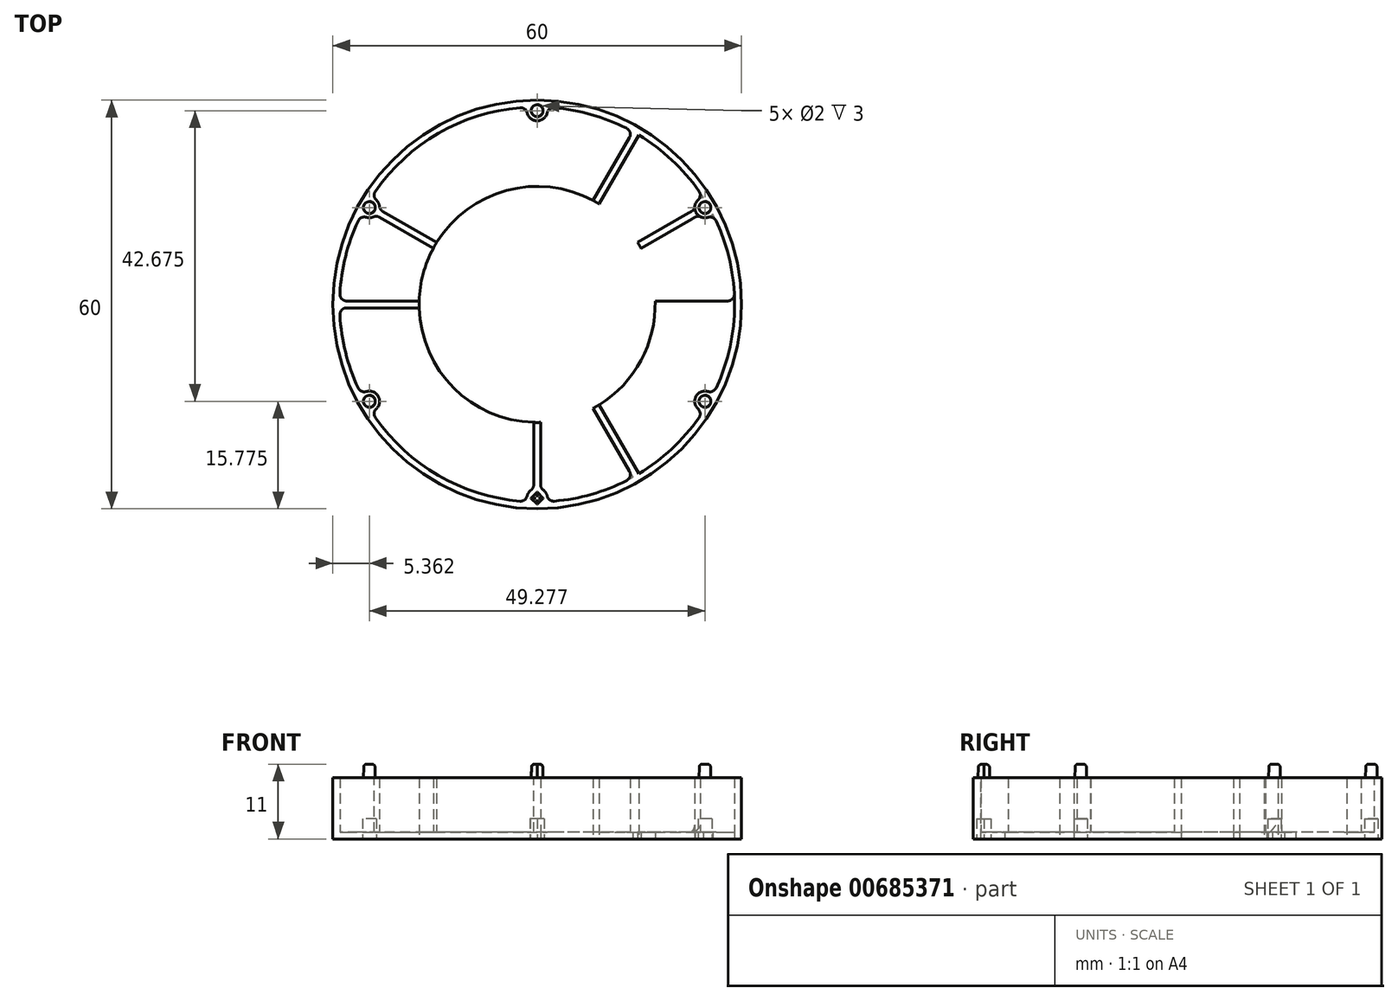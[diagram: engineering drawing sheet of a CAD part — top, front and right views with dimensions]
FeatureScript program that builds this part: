
annotation { "Feature Type Name" : "Feature", "Feature Type Description" : "" }
export const myFeature = defineFeature(function(context is Context, id is Id, definition is map)
    precondition{}
    {
        {
            var Q0;
            Q0=qCreatedBy(makeId("Top.planeOp"),FACE);
            var sketch = newSketch(context, id + "F0", { "sketchPlane" : qUnion([Q0])});
            skCircle(sketch, "E0", {"center": v(0, 0) * mm, "radius": 30 * mm});
            skCircle(sketch, "E1.0", {"center": v(0, 0) * mm, "radius": 29 * mm});
            skLineSegment(sketch, "E2.bottom", {"start": v(14.56, 26.23) * mm, "end": v(15.43, 25.73) * mm});
            skLineSegment(sketch, "E2.top", {"start": v(-15.43, -25.73) * mm, "end": v(-14.56, -26.23) * mm});
            skLineSegment(sketch, "E2.left", {"start": v(14.56, 26.23) * mm, "end": v(-15.43, -25.73) * mm});
            skLineSegment(sketch, "E2.right", {"start": v(15.43, 25.73) * mm, "end": v(-14.56, -26.23) * mm});
            skLineSegment(sketch, "E3.bottom", {"start": v(25.73, 15.43) * mm, "end": v(26.23, 14.56) * mm});
            skLineSegment(sketch, "E3.top", {"start": v(-26.23, -14.56) * mm, "end": v(-25.73, -15.43) * mm});
            skLineSegment(sketch, "E3.left", {"start": v(25.73, 15.43) * mm, "end": v(-26.23, -14.56) * mm});
            skLineSegment(sketch, "E3.right", {"start": v(26.23, 14.56) * mm, "end": v(-25.73, -15.43) * mm});
            skLineSegment(sketch, "E4", {"start": v(-38.35, 0) * mm, "end": v(39.17, 0) * mm, "construction": true});
            skLineSegment(sketch, "E5", {"start": v(0, 42.5) * mm, "end": v(0, -42.47) * mm, "construction": true});
            skLineSegment(sketch, "E6.bottom", {"start": v(-30, 0.5) * mm, "end": v(30, 0.5) * mm});
            skLineSegment(sketch, "E6.top", {"start": v(-30, -0.5) * mm, "end": v(30, -0.5) * mm});
            skLineSegment(sketch, "E6.left", {"start": v(-30, 0.5) * mm, "end": v(-30, -0.5) * mm});
            skLineSegment(sketch, "E6.right", {"start": v(30, 0.5) * mm, "end": v(30, -0.5) * mm});
            skLineSegment(sketch, "E7.bottom", {"start": v(-25.73, 15.43) * mm, "end": v(26.23, -14.56) * mm});
            skLineSegment(sketch, "E7.top", {"start": v(-26.23, 14.56) * mm, "end": v(25.73, -15.43) * mm});
            skLineSegment(sketch, "E7.left", {"start": v(-25.73, 15.43) * mm, "end": v(-26.23, 14.56) * mm});
            skLineSegment(sketch, "E7.right", {"start": v(26.23, -14.56) * mm, "end": v(25.73, -15.43) * mm});
            skLineSegment(sketch, "E8.bottom", {"start": v(-0.5, 30) * mm, "end": v(0.5, 30) * mm});
            skLineSegment(sketch, "E8.top", {"start": v(-0.5, -30) * mm, "end": v(0.5, -30) * mm});
            skLineSegment(sketch, "E8.left", {"start": v(-0.5, 30) * mm, "end": v(-0.5, -30) * mm});
            skLineSegment(sketch, "E8.right", {"start": v(0.5, 30) * mm, "end": v(0.5, -30) * mm});
            skLineSegment(sketch, "E9.bottom", {"start": v(-15.43, 25.73) * mm, "end": v(-14.56, 26.23) * mm});
            skLineSegment(sketch, "E9.top", {"start": v(14.56, -26.23) * mm, "end": v(15.43, -25.73) * mm});
            skLineSegment(sketch, "E9.left", {"start": v(-15.43, 25.73) * mm, "end": v(14.56, -26.23) * mm});
            skLineSegment(sketch, "E9.right", {"start": v(-14.56, 26.23) * mm, "end": v(15.43, -25.73) * mm});
            skCircle(sketch, "E10", {"center": v(0, 0) * mm, "radius": 17.33 * mm});
            skSolve(sketch);
        }
        {
            var Q0;
            Q0=qCreatedBy(makeId("Top.planeOp"),FACE);
            var sketch = newSketch(context, id + "F1", { "sketchPlane" : qUnion([Q0])});
            skCircle(sketch, "E11", {"center": v(0, 0) * mm, "radius": 30 * mm});
            skCircle(sketch, "E12", {"center": v(0, 0) * mm, "radius": 29 * mm});
            skSolve(sketch);
        }
        {
            var Q0;
            Q0=makeQuery(id+"F1.imprint","IMPRINT",FACE,{"disambiguationData":[TD([[makeQuery(id+"F1.imprint","IMPRINT",EDGE,{"derivedFrom":sQuery(id+"F1.wireOp",EDGE,"E11")}),1.0]])]});
            extrude(context, id + "F2", {"entities" : qUnion([Q0]), "depth" : 9 * mm, "offsetDistance" : 25 * mm});
        }
        {
            var Q0;
            {var subQ0=sQuery(id+"F0.wireOp",EDGE,"E7.bottom");var subQ1=sQuery(id+"F0.wireOp",EDGE,"E1.0");var subQ2=makeQuery(id+"F0.imprint","INTERSECT",VERTEX,{"disambiguationData":[OD(0.0)],"derivedFrom":[subQ1,subQ0]});Q0=makeQuery(id+"F0.imprint","IMPRINT",FACE,{"disambiguationData":[TD([[makeQuery(id+"F0.imprint","IMPRINT",EDGE,{"disambiguationData":[TD([[subQ2,-1.0]])],"derivedFrom":subQ1}),1.0]])]});}
            var Q1;
            {var subQ0=sQuery(id+"F0.wireOp",EDGE,"E2.right");var subQ1=sQuery(id+"F0.wireOp",EDGE,"E1.0");var subQ2=makeQuery(id+"F0.imprint","INTERSECT",VERTEX,{"disambiguationData":[OD(0.0)],"derivedFrom":[subQ1,subQ0]});Q1=makeQuery(id+"F0.imprint","IMPRINT",FACE,{"disambiguationData":[TD([[makeQuery(id+"F0.imprint","IMPRINT",EDGE,{"disambiguationData":[TD([[subQ2,-1.0]])],"derivedFrom":subQ1}),1.0]])]});}
            var Q2;
            {var subQ0=sQuery(id+"F0.wireOp",EDGE,"E8.left");var subQ1=sQuery(id+"F0.wireOp",EDGE,"E1.0");var subQ2=makeQuery(id+"F0.imprint","INTERSECT",VERTEX,{"disambiguationData":[OD(1.0)],"derivedFrom":[subQ1,subQ0]});Q2=makeQuery(id+"F0.imprint","IMPRINT",FACE,{"disambiguationData":[TD([[makeQuery(id+"F0.imprint","IMPRINT",EDGE,{"disambiguationData":[TD([[subQ2,-1.0]])],"derivedFrom":subQ1}),1.0]])]});}
            var Q3;
            {var subQ0=sQuery(id+"F0.wireOp",EDGE,"E9.left");var subQ1=sQuery(id+"F0.wireOp",EDGE,"E1.0");var subQ2=makeQuery(id+"F0.imprint","INTERSECT",VERTEX,{"disambiguationData":[OD(1.0)],"derivedFrom":[subQ1,subQ0]});Q3=makeQuery(id+"F0.imprint","IMPRINT",FACE,{"disambiguationData":[TD([[makeQuery(id+"F0.imprint","IMPRINT",EDGE,{"disambiguationData":[TD([[subQ2,-1.0]])],"derivedFrom":subQ1}),1.0]])]});}
            var Q4;
            {var subQ0=sQuery(id+"F0.wireOp",EDGE,"E6.bottom");var subQ1=sQuery(id+"F0.wireOp",EDGE,"E1.0");var subQ2=makeQuery(id+"F0.imprint","INTERSECT",VERTEX,{"disambiguationData":[OD(1.0)],"derivedFrom":[subQ1,subQ0]});Q4=makeQuery(id+"F0.imprint","IMPRINT",FACE,{"disambiguationData":[TD([[makeQuery(id+"F0.imprint","IMPRINT",EDGE,{"disambiguationData":[TD([[subQ2,-1.0]])],"derivedFrom":subQ1}),1.0]])]});}
            extrude(context, id + "F3", {"entities" : qUnion([Q0, Q1, Q2, Q3, Q4]), "operationType" : NewBodyOperationType.ADD, "depth" : 9 * mm, "offsetDistance" : 25 * mm});
        }
        {
            var Q0;
            Q0=makeQuery(id+"F1.imprint","IMPRINT",FACE,{"disambiguationData":[TD([[makeQuery(id+"F1.imprint","IMPRINT",EDGE,{"derivedFrom":sQuery(id+"F1.wireOp",EDGE,"E11")}),1.0]])]});
            var Q1;
            Q1=makeQuery(id+"F1.imprint","IMPRINT",FACE,{"disambiguationData":[TD([[makeQuery(id+"F1.imprint","IMPRINT",EDGE,{"derivedFrom":sQuery(id+"F1.wireOp",EDGE,"E12")}),1.0]])]});
            extrude(context, id + "F4", {"entities" : qUnion([Q0, Q1]), "operationType" : NewBodyOperationType.ADD, "depth" : 1 * mm, "offsetDistance" : 25 * mm});
        }
        {
            var Q0;
            {var subQ0=sQuery(id+"F0.wireOp",EDGE,"E8.right");var subQ1=sQuery(id+"F0.wireOp",EDGE,"E1.0");var subQ2=makeQuery(id+"F0.imprint","INTERSECT",VERTEX,{"disambiguationData":[OD(1.0)],"derivedFrom":[subQ1,subQ0]});Q0=makeQuery(id+"F0.imprint","IMPRINT",FACE,{"disambiguationData":[TD([[makeQuery(id+"F0.imprint","IMPRINT",EDGE,{"disambiguationData":[TD([[subQ2,-1.0]])],"derivedFrom":subQ1}),1.0]])]});}
            var Q1;
            {var subQ0=sQuery(id+"F0.wireOp",EDGE,"E3.right");var subQ1=sQuery(id+"F0.wireOp",EDGE,"E1.0");var subQ2=makeQuery(id+"F0.imprint","INTERSECT",VERTEX,{"disambiguationData":[OD(0.0)],"derivedFrom":[subQ1,subQ0]});Q1=makeQuery(id+"F0.imprint","IMPRINT",FACE,{"disambiguationData":[TD([[makeQuery(id+"F0.imprint","IMPRINT",EDGE,{"disambiguationData":[TD([[subQ2,1.0]])],"derivedFrom":subQ1}),1.0]])]});}
            var Q2;
            {var subQ0=sQuery(id+"F0.wireOp",EDGE,"E3.left");var subQ1=sQuery(id+"F0.wireOp",EDGE,"E1.0");var subQ2=makeQuery(id+"F0.imprint","INTERSECT",VERTEX,{"disambiguationData":[OD(0.0)],"derivedFrom":[subQ1,subQ0]});Q2=makeQuery(id+"F0.imprint","IMPRINT",FACE,{"disambiguationData":[TD([[makeQuery(id+"F0.imprint","IMPRINT",EDGE,{"disambiguationData":[TD([[subQ2,-1.0]])],"derivedFrom":subQ1}),1.0]])]});}
            extrude(context, id + "F5", {"entities" : qUnion([Q0, Q1, Q2]), "operationType" : NewBodyOperationType.REMOVE, "depth" : 1 * mm, "offsetDistance" : 25 * mm});
        }
        {
            var Q0;
            Q0=qCreatedBy(makeId("Top.planeOp"),FACE);
            var sketch = newSketch(context, id + "F6", { "sketchPlane" : qUnion([Q0])});
            skCircle(sketch, "E13", {"center": v(0, 0) * mm, "radius": 28.45 * mm});
            skLineSegment(sketch, "E14", {"start": v(0, 28.45) * mm, "end": v(0, -28.45) * mm, "construction": true});
            skLineSegment(sketch, "E15", {"start": v(24.64, 14.22) * mm, "end": v(0, 0) * mm, "construction": true});
            skLineSegment(sketch, "E16", {"start": v(14.23, 24.64) * mm, "end": v(0, 0) * mm, "construction": true});
            skLineSegment(sketch, "E17", {"start": v(0, 0) * mm, "end": v(28.45, 0) * mm, "construction": true});
            skLineSegment(sketch, "E18", {"start": v(0, 0) * mm, "end": v(24.64, -14.22) * mm, "construction": true});
            skLineSegment(sketch, "E19", {"start": v(0, 0) * mm, "end": v(14.23, -24.64) * mm, "construction": true});
            skLineSegment(sketch, "E20", {"start": v(0, 0) * mm, "end": v(-14.23, 24.64) * mm, "construction": true});
            skLineSegment(sketch, "E21", {"start": v(0, 0) * mm, "end": v(-24.64, 14.22) * mm, "construction": true});
            skLineSegment(sketch, "E22", {"start": v(0, 0) * mm, "end": v(-28.45, 0) * mm, "construction": true});
            skLineSegment(sketch, "E23", {"start": v(0, 0) * mm, "end": v(-24.64, -14.23) * mm, "construction": true});
            skLineSegment(sketch, "E24", {"start": v(0, 0) * mm, "end": v(-14.22, -24.64) * mm, "construction": true});
            skCircle(sketch, "E25", {"center": v(0, 28.45) * mm, "radius": 1.5 * mm});
            skCircle(sketch, "E26", {"center": v(24.64, 14.22) * mm, "radius": 1.5 * mm});
            skCircle(sketch, "E27", {"center": v(24.64, -14.22) * mm, "radius": 1.5 * mm});
            skCircle(sketch, "E28", {"center": v(0, -28.45) * mm, "radius": 1.5 * mm});
            skCircle(sketch, "E29", {"center": v(-24.64, -14.23) * mm, "radius": 1.5 * mm});
            skCircle(sketch, "E30", {"center": v(-24.64, 14.22) * mm, "radius": 1.5 * mm});
            skCircle(sketch, "E31", {"center": v(-24.64, 14.22) * mm, "radius": 1 * mm});
            skCircle(sketch, "E32", {"center": v(0, 28.45) * mm, "radius": 1 * mm});
            skCircle(sketch, "E33", {"center": v(24.64, 14.22) * mm, "radius": 1 * mm});
            skCircle(sketch, "E34", {"center": v(24.64, -14.22) * mm, "radius": 1 * mm});
            skCircle(sketch, "E35", {"center": v(-24.64, -14.23) * mm, "radius": 1 * mm});
            skLineSegment(sketch, "E36.bottom", {"start": v(1.06, -28.45) * mm, "end": v(0, -29.51) * mm});
            skLineSegment(sketch, "E36.top", {"start": v(0, -27.39) * mm, "end": v(-1.06, -28.45) * mm});
            skLineSegment(sketch, "E36.left", {"start": v(1.06, -28.45) * mm, "end": v(0, -27.39) * mm});
            skLineSegment(sketch, "E36.right", {"start": v(0, -29.51) * mm, "end": v(-1.06, -28.45) * mm});
            skSolve(sketch);
        }
        {
            var Q0;
            {var subQ0=sQuery(id+"F6.wireOp",EDGE,"E30");var subQ1=sQuery(id+"F6.wireOp",EDGE,"E13");var subQ2=makeQuery(id+"F6.imprint","INTERSECT",VERTEX,{"disambiguationData":[OD(0.0)],"derivedFrom":[subQ1,subQ0]});Q0=makeQuery(id+"F6.imprint","IMPRINT",FACE,{"disambiguationData":[TD([[makeQuery(id+"F6.imprint","IMPRINT",EDGE,{"disambiguationData":[TD([[subQ2,-1.0]])],"derivedFrom":subQ1}),1.0]])]});}
            var Q1;
            {var subQ0=sQuery(id+"F6.wireOp",EDGE,"E30");var subQ1=sQuery(id+"F6.wireOp",EDGE,"E13");var subQ2=makeQuery(id+"F6.imprint","INTERSECT",VERTEX,{"disambiguationData":[OD(0.0)],"derivedFrom":[subQ1,subQ0]});Q1=makeQuery(id+"F6.imprint","IMPRINT",FACE,{"disambiguationData":[TD([[makeQuery(id+"F6.imprint","IMPRINT",EDGE,{"disambiguationData":[TD([[subQ2,-1.0]])],"derivedFrom":subQ1}),-1.0]])]});}
            var Q2;
            {var subQ0=sQuery(id+"F6.wireOp",EDGE,"E25");var subQ1=sQuery(id+"F6.wireOp",EDGE,"E13");var subQ2=makeQuery(id+"F6.imprint","INTERSECT",VERTEX,{"disambiguationData":[OD(0.0)],"derivedFrom":[subQ1,subQ0]});Q2=makeQuery(id+"F6.imprint","IMPRINT",FACE,{"disambiguationData":[TD([[makeQuery(id+"F6.imprint","IMPRINT",EDGE,{"disambiguationData":[TD([[subQ2,-1.0]])],"derivedFrom":subQ1}),1.0]])]});}
            var Q3;
            {var subQ0=sQuery(id+"F6.wireOp",EDGE,"E25");var subQ1=sQuery(id+"F6.wireOp",EDGE,"E13");var subQ2=makeQuery(id+"F6.imprint","INTERSECT",VERTEX,{"disambiguationData":[OD(0.0)],"derivedFrom":[subQ1,subQ0]});Q3=makeQuery(id+"F6.imprint","IMPRINT",FACE,{"disambiguationData":[TD([[makeQuery(id+"F6.imprint","IMPRINT",EDGE,{"disambiguationData":[TD([[subQ2,-1.0]])],"derivedFrom":subQ1}),-1.0]])]});}
            var Q4;
            {var subQ0=sQuery(id+"F6.wireOp",EDGE,"E26");var subQ1=sQuery(id+"F6.wireOp",EDGE,"E13");var subQ2=makeQuery(id+"F6.imprint","INTERSECT",VERTEX,{"disambiguationData":[OD(0.0)],"derivedFrom":[subQ1,subQ0]});Q4=makeQuery(id+"F6.imprint","IMPRINT",FACE,{"disambiguationData":[TD([[makeQuery(id+"F6.imprint","IMPRINT",EDGE,{"disambiguationData":[TD([[subQ2,-1.0]])],"derivedFrom":subQ1}),-1.0]])]});}
            var Q5;
            {var subQ0=sQuery(id+"F6.wireOp",EDGE,"E26");var subQ1=sQuery(id+"F6.wireOp",EDGE,"E13");var subQ2=makeQuery(id+"F6.imprint","INTERSECT",VERTEX,{"disambiguationData":[OD(0.0)],"derivedFrom":[subQ1,subQ0]});Q5=makeQuery(id+"F6.imprint","IMPRINT",FACE,{"disambiguationData":[TD([[makeQuery(id+"F6.imprint","IMPRINT",EDGE,{"disambiguationData":[TD([[subQ2,-1.0]])],"derivedFrom":subQ1}),1.0]])]});}
            var Q6;
            {var subQ0=sQuery(id+"F6.wireOp",EDGE,"E29");var subQ1=sQuery(id+"F6.wireOp",EDGE,"E13");var subQ2=makeQuery(id+"F6.imprint","INTERSECT",VERTEX,{"disambiguationData":[OD(0.0)],"derivedFrom":[subQ1,subQ0]});Q6=makeQuery(id+"F6.imprint","IMPRINT",FACE,{"disambiguationData":[TD([[makeQuery(id+"F6.imprint","IMPRINT",EDGE,{"disambiguationData":[TD([[subQ2,-1.0]])],"derivedFrom":subQ1}),1.0]])]});}
            var Q7;
            {var subQ0=sQuery(id+"F6.wireOp",EDGE,"E29");var subQ1=sQuery(id+"F6.wireOp",EDGE,"E13");var subQ2=makeQuery(id+"F6.imprint","INTERSECT",VERTEX,{"disambiguationData":[OD(0.0)],"derivedFrom":[subQ1,subQ0]});Q7=makeQuery(id+"F6.imprint","IMPRINT",FACE,{"disambiguationData":[TD([[makeQuery(id+"F6.imprint","IMPRINT",EDGE,{"disambiguationData":[TD([[subQ2,-1.0]])],"derivedFrom":subQ1}),-1.0]])]});}
            var Q8;
            {var subQ3=sQuery(id+"F6.wireOp",EDGE,"E13");var subQ5=sQuery(id+"F6.wireOp",EDGE,"E28");var subQ6=makeQuery(id+"F6.imprint","INTERSECT",VERTEX,{"disambiguationData":[OD(0.0)],"derivedFrom":[subQ3,subQ5]});Q8=makeQuery(id+"F6.imprint","IMPRINT",FACE,{"disambiguationData":[TD([[makeQuery(id+"F6.imprint","IMPRINT",EDGE,{"disambiguationData":[TD([[subQ6,-1.0]])],"derivedFrom":subQ3}),1.0]])]});}
            var Q9;
            {var subQ6=sQuery(id+"F6.wireOp",EDGE,"E36.bottom");Q9=makeQuery(id+"F6.imprint","IMPRINT",FACE,{"disambiguationData":[TD([[makeQuery(id+"F6.imprint","IMPRINT",EDGE,{"derivedFrom":subQ6}),1.0]])]});}
            var Q10;
            {var subQ0=sQuery(id+"F6.wireOp",EDGE,"E27");var subQ1=sQuery(id+"F6.wireOp",EDGE,"E13");var subQ2=makeQuery(id+"F6.imprint","INTERSECT",VERTEX,{"disambiguationData":[OD(0.0)],"derivedFrom":[subQ1,subQ0]});Q10=makeQuery(id+"F6.imprint","IMPRINT",FACE,{"disambiguationData":[TD([[makeQuery(id+"F6.imprint","IMPRINT",EDGE,{"disambiguationData":[TD([[subQ2,-1.0]])],"derivedFrom":subQ1}),-1.0]])]});}
            var Q11;
            {var subQ0=sQuery(id+"F6.wireOp",EDGE,"E27");var subQ1=sQuery(id+"F6.wireOp",EDGE,"E13");var subQ2=makeQuery(id+"F6.imprint","INTERSECT",VERTEX,{"disambiguationData":[OD(0.0)],"derivedFrom":[subQ1,subQ0]});Q11=makeQuery(id+"F6.imprint","IMPRINT",FACE,{"disambiguationData":[TD([[makeQuery(id+"F6.imprint","IMPRINT",EDGE,{"disambiguationData":[TD([[subQ2,-1.0]])],"derivedFrom":subQ1}),1.0]])]});}
            var Q12;
            {var subQ0=sQuery(id+"F6.wireOp",EDGE,"E31");var subQ1=sQuery(id+"F6.wireOp",EDGE,"E13");var subQ2=makeQuery(id+"F6.imprint","INTERSECT",VERTEX,{"disambiguationData":[OD(0.0)],"derivedFrom":[subQ1,subQ0]});Q12=makeQuery(id+"F6.imprint","IMPRINT",FACE,{"disambiguationData":[TD([[makeQuery(id+"F6.imprint","IMPRINT",EDGE,{"disambiguationData":[TD([[subQ2,-1.0]])],"derivedFrom":subQ1}),1.0]])]});}
            var Q13;
            {var subQ0=sQuery(id+"F6.wireOp",EDGE,"E31");var subQ1=sQuery(id+"F6.wireOp",EDGE,"E13");var subQ2=makeQuery(id+"F6.imprint","INTERSECT",VERTEX,{"disambiguationData":[OD(0.0)],"derivedFrom":[subQ1,subQ0]});Q13=makeQuery(id+"F6.imprint","IMPRINT",FACE,{"disambiguationData":[TD([[makeQuery(id+"F6.imprint","IMPRINT",EDGE,{"disambiguationData":[TD([[subQ2,-1.0]])],"derivedFrom":subQ1}),-1.0]])]});}
            var Q14;
            {var subQ0=sQuery(id+"F6.wireOp",EDGE,"E32");var subQ1=sQuery(id+"F6.wireOp",EDGE,"E13");var subQ2=makeQuery(id+"F6.imprint","INTERSECT",VERTEX,{"disambiguationData":[OD(0.0)],"derivedFrom":[subQ1,subQ0]});Q14=makeQuery(id+"F6.imprint","IMPRINT",FACE,{"disambiguationData":[TD([[makeQuery(id+"F6.imprint","IMPRINT",EDGE,{"disambiguationData":[TD([[subQ2,-1.0]])],"derivedFrom":subQ1}),-1.0]])]});}
            var Q15;
            {var subQ0=sQuery(id+"F6.wireOp",EDGE,"E32");var subQ1=sQuery(id+"F6.wireOp",EDGE,"E13");var subQ2=makeQuery(id+"F6.imprint","INTERSECT",VERTEX,{"disambiguationData":[OD(0.0)],"derivedFrom":[subQ1,subQ0]});Q15=makeQuery(id+"F6.imprint","IMPRINT",FACE,{"disambiguationData":[TD([[makeQuery(id+"F6.imprint","IMPRINT",EDGE,{"disambiguationData":[TD([[subQ2,-1.0]])],"derivedFrom":subQ1}),1.0]])]});}
            var Q16;
            {var subQ0=sQuery(id+"F6.wireOp",EDGE,"E33");var subQ1=sQuery(id+"F6.wireOp",EDGE,"E13");var subQ2=makeQuery(id+"F6.imprint","INTERSECT",VERTEX,{"disambiguationData":[OD(0.0)],"derivedFrom":[subQ1,subQ0]});Q16=makeQuery(id+"F6.imprint","IMPRINT",FACE,{"disambiguationData":[TD([[makeQuery(id+"F6.imprint","IMPRINT",EDGE,{"disambiguationData":[TD([[subQ2,-1.0]])],"derivedFrom":subQ1}),-1.0]])]});}
            var Q17;
            {var subQ0=sQuery(id+"F6.wireOp",EDGE,"E33");var subQ1=sQuery(id+"F6.wireOp",EDGE,"E13");var subQ2=makeQuery(id+"F6.imprint","INTERSECT",VERTEX,{"disambiguationData":[OD(0.0)],"derivedFrom":[subQ1,subQ0]});Q17=makeQuery(id+"F6.imprint","IMPRINT",FACE,{"disambiguationData":[TD([[makeQuery(id+"F6.imprint","IMPRINT",EDGE,{"disambiguationData":[TD([[subQ2,-1.0]])],"derivedFrom":subQ1}),1.0]])]});}
            var Q18;
            {var subQ0=sQuery(id+"F6.wireOp",EDGE,"E34");var subQ1=sQuery(id+"F6.wireOp",EDGE,"E13");var subQ2=makeQuery(id+"F6.imprint","INTERSECT",VERTEX,{"disambiguationData":[OD(0.0)],"derivedFrom":[subQ1,subQ0]});Q18=makeQuery(id+"F6.imprint","IMPRINT",FACE,{"disambiguationData":[TD([[makeQuery(id+"F6.imprint","IMPRINT",EDGE,{"disambiguationData":[TD([[subQ2,-1.0]])],"derivedFrom":subQ1}),-1.0]])]});}
            var Q19;
            {var subQ0=sQuery(id+"F6.wireOp",EDGE,"E34");var subQ1=sQuery(id+"F6.wireOp",EDGE,"E13");var subQ2=makeQuery(id+"F6.imprint","INTERSECT",VERTEX,{"disambiguationData":[OD(0.0)],"derivedFrom":[subQ1,subQ0]});Q19=makeQuery(id+"F6.imprint","IMPRINT",FACE,{"disambiguationData":[TD([[makeQuery(id+"F6.imprint","IMPRINT",EDGE,{"disambiguationData":[TD([[subQ2,-1.0]])],"derivedFrom":subQ1}),1.0]])]});}
            var Q20;
            {var subQ1=sQuery(id+"F6.wireOp",EDGE,"E36.bottom");Q20=makeQuery(id+"F6.imprint","IMPRINT",FACE,{"disambiguationData":[TD([[makeQuery(id+"F6.imprint","IMPRINT",EDGE,{"derivedFrom":subQ1}),-1.0]])]});}
            var Q21;
            {var subQ0=sQuery(id+"F6.wireOp",EDGE,"E35");var subQ1=sQuery(id+"F6.wireOp",EDGE,"E13");var subQ2=makeQuery(id+"F6.imprint","INTERSECT",VERTEX,{"disambiguationData":[OD(0.0)],"derivedFrom":[subQ1,subQ0]});Q21=makeQuery(id+"F6.imprint","IMPRINT",FACE,{"disambiguationData":[TD([[makeQuery(id+"F6.imprint","IMPRINT",EDGE,{"disambiguationData":[TD([[subQ2,-1.0]])],"derivedFrom":subQ1}),-1.0]])]});}
            var Q22;
            {var subQ0=sQuery(id+"F6.wireOp",EDGE,"E35");var subQ1=sQuery(id+"F6.wireOp",EDGE,"E13");var subQ2=makeQuery(id+"F6.imprint","INTERSECT",VERTEX,{"disambiguationData":[OD(0.0)],"derivedFrom":[subQ1,subQ0]});Q22=makeQuery(id+"F6.imprint","IMPRINT",FACE,{"disambiguationData":[TD([[makeQuery(id+"F6.imprint","IMPRINT",EDGE,{"disambiguationData":[TD([[subQ2,-1.0]])],"derivedFrom":subQ1}),1.0]])]});}
            var Q23;
            {var subQ0=sQuery(id+"F6.wireOp",EDGE,"E36.top");var subQ1=sQuery(id+"F6.wireOp",EDGE,"E13");var subQ2=makeQuery(id+"F6.imprint","INTERSECT",VERTEX,{"derivedFrom":[subQ1,subQ0]});Q23=makeQuery(id+"F6.imprint","IMPRINT",FACE,{"disambiguationData":[TD([[makeQuery(id+"F6.imprint","IMPRINT",EDGE,{"disambiguationData":[TD([[subQ2,-1.0]])],"derivedFrom":subQ1}),1.0]])]});}
            extrude(context, id + "F7", {"entities" : qUnion([Q0, Q1, Q2, Q3, Q4, Q5, Q6, Q7, Q8, Q9, Q10, Q11, Q12, Q13, Q14, Q15, Q16, Q17, Q18, Q19, Q20, Q21, Q22, Q23]), "operationType" : NewBodyOperationType.ADD, "depth" : 9 * mm, "offsetDistance" : 25 * mm});
        }
        {
            var Q0;
            {var subQ0=sQuery(id+"F0.wireOp",EDGE,"E8.right");var subQ1=sQuery(id+"F0.wireOp",EDGE,"E1.0");Q0=makeQuery(id+"F3.opExtrude","SWEPT_EDGE",EDGE,{"disambiguationData":[OSD([subQ1,subQ0]),TDD([makeQuery(id+"F0.imprint","INTERSECT",VERTEX,{"disambiguationData":[OD(1.0)],"derivedFrom":[subQ1,subQ0]})])]});}
            var Q1;
            {var subQ0=sQuery(id+"F0.wireOp",EDGE,"E2.left");var subQ1=sQuery(id+"F0.wireOp",EDGE,"E1.0");Q1=makeQuery(id+"F3.opExtrude","SWEPT_EDGE",EDGE,{"disambiguationData":[OSD([subQ1,subQ0]),TDD([makeQuery(id+"F0.imprint","INTERSECT",VERTEX,{"disambiguationData":[OD(1.0)],"derivedFrom":[subQ1,subQ0]})])]});}
            var Q2;
            {var subQ0=sQuery(id+"F0.wireOp",EDGE,"E3.left");var subQ1=sQuery(id+"F0.wireOp",EDGE,"E1.0");Q2=makeQuery(id+"F3.opExtrude","SWEPT_EDGE",EDGE,{"disambiguationData":[OSD([subQ1,subQ0]),TDD([makeQuery(id+"F0.imprint","INTERSECT",VERTEX,{"disambiguationData":[OD(1.0)],"derivedFrom":[subQ1,subQ0]})])]});}
            var Q3;
            {var subQ0=sQuery(id+"F0.wireOp",EDGE,"E6.bottom");var subQ1=sQuery(id+"F0.wireOp",EDGE,"E1.0");Q3=makeQuery(id+"F3.opExtrude","SWEPT_EDGE",EDGE,{"disambiguationData":[OSD([subQ1,subQ0]),TDD([makeQuery(id+"F0.imprint","INTERSECT",VERTEX,{"disambiguationData":[OD(1.0)],"derivedFrom":[subQ1,subQ0]})])]});}
            var Q4;
            {var subQ0=sQuery(id+"F0.wireOp",EDGE,"E9.right");var subQ1=sQuery(id+"F0.wireOp",EDGE,"E1.0");Q4=makeQuery(id+"F3.opExtrude","SWEPT_EDGE",EDGE,{"disambiguationData":[OSD([subQ1,subQ0]),TDD([makeQuery(id+"F0.imprint","INTERSECT",VERTEX,{"disambiguationData":[OD(1.0)],"derivedFrom":[subQ1,subQ0]})])]});}
            var Q5;
            {var subQ0=sQuery(id+"F0.wireOp",EDGE,"E7.bottom");var subQ1=sQuery(id+"F0.wireOp",EDGE,"E1.0");Q5=makeQuery(id+"F3.opExtrude","SWEPT_EDGE",EDGE,{"disambiguationData":[OSD([subQ1,subQ0]),TDD([makeQuery(id+"F0.imprint","INTERSECT",VERTEX,{"disambiguationData":[OD(1.0)],"derivedFrom":[subQ1,subQ0]})])]});}
            var Q6;
            {var subQ0=sQuery(id+"F0.wireOp",EDGE,"E8.left");var subQ1=sQuery(id+"F0.wireOp",EDGE,"E1.0");Q6=makeQuery(id+"F3.opExtrude","SWEPT_EDGE",EDGE,{"disambiguationData":[OSD([subQ1,subQ0]),TDD([makeQuery(id+"F0.imprint","INTERSECT",VERTEX,{"disambiguationData":[OD(0.0)],"derivedFrom":[subQ1,subQ0]})])]});}
            var Q7;
            {var subQ0=sQuery(id+"F0.wireOp",EDGE,"E2.left");var subQ1=sQuery(id+"F0.wireOp",EDGE,"E1.0");Q7=makeQuery(id+"F3.opExtrude","SWEPT_EDGE",EDGE,{"disambiguationData":[OSD([subQ1,subQ0]),TDD([makeQuery(id+"F0.imprint","INTERSECT",VERTEX,{"disambiguationData":[OD(0.0)],"derivedFrom":[subQ1,subQ0]})])]});}
            var Q8;
            {var subQ0=sQuery(id+"F0.wireOp",EDGE,"E3.left");var subQ1=sQuery(id+"F0.wireOp",EDGE,"E1.0");Q8=makeQuery(id+"F3.opExtrude","SWEPT_EDGE",EDGE,{"disambiguationData":[OSD([subQ1,subQ0]),TDD([makeQuery(id+"F0.imprint","INTERSECT",VERTEX,{"disambiguationData":[OD(0.0)],"derivedFrom":[subQ1,subQ0]})])]});}
            var Q9;
            {var subQ0=sQuery(id+"F0.wireOp",EDGE,"E6.top");var subQ1=sQuery(id+"F0.wireOp",EDGE,"E1.0");Q9=makeQuery(id+"F3.opExtrude","SWEPT_EDGE",EDGE,{"disambiguationData":[OSD([subQ1,subQ0]),TDD([makeQuery(id+"F0.imprint","INTERSECT",VERTEX,{"disambiguationData":[OD(1.0)],"derivedFrom":[subQ1,subQ0]})])]});}
            var Q10;
            {var subQ0=sQuery(id+"F0.wireOp",EDGE,"E7.top");var subQ1=sQuery(id+"F0.wireOp",EDGE,"E1.0");Q10=makeQuery(id+"F3.opExtrude","SWEPT_EDGE",EDGE,{"disambiguationData":[OSD([subQ1,subQ0]),TDD([makeQuery(id+"F0.imprint","INTERSECT",VERTEX,{"disambiguationData":[OD(0.0)],"derivedFrom":[subQ1,subQ0]})])]});}
            var Q11;
            {var subQ0=sQuery(id+"F0.wireOp",EDGE,"E6.top");var subQ1=sQuery(id+"F0.wireOp",EDGE,"E1.0");Q11=makeQuery(id+"F3.opExtrude","SWEPT_EDGE",EDGE,{"disambiguationData":[OSD([subQ1,subQ0]),TDD([makeQuery(id+"F0.imprint","INTERSECT",VERTEX,{"disambiguationData":[OD(0.0)],"derivedFrom":[subQ1,subQ0]})])]});}
            var Q12;
            {var subQ0=sQuery(id+"F0.wireOp",EDGE,"E9.left");var subQ1=sQuery(id+"F0.wireOp",EDGE,"E1.0");Q12=makeQuery(id+"F3.opExtrude","SWEPT_EDGE",EDGE,{"disambiguationData":[OSD([subQ1,subQ0]),TDD([makeQuery(id+"F0.imprint","INTERSECT",VERTEX,{"disambiguationData":[OD(0.0)],"derivedFrom":[subQ1,subQ0]})])]});}
            var Q13;
            {var subQ0=sQuery(id+"F0.wireOp",EDGE,"E8.right");var subQ1=sQuery(id+"F0.wireOp",EDGE,"E1.0");Q13=makeQuery(id+"F3.opExtrude","SWEPT_EDGE",EDGE,{"disambiguationData":[OSD([subQ1,subQ0]),TDD([makeQuery(id+"F0.imprint","INTERSECT",VERTEX,{"disambiguationData":[OD(0.0)],"derivedFrom":[subQ1,subQ0]})])]});}
            var Q14;
            {var subQ0=sQuery(id+"F0.wireOp",EDGE,"E7.bottom");var subQ1=sQuery(id+"F0.wireOp",EDGE,"E1.0");Q14=makeQuery(id+"F3.opExtrude","SWEPT_EDGE",EDGE,{"disambiguationData":[OSD([subQ1,subQ0]),TDD([makeQuery(id+"F0.imprint","INTERSECT",VERTEX,{"disambiguationData":[OD(0.0)],"derivedFrom":[subQ1,subQ0]})])]});}
            var Q15;
            {var subQ0=sQuery(id+"F0.wireOp",EDGE,"E9.right");var subQ1=sQuery(id+"F0.wireOp",EDGE,"E1.0");Q15=makeQuery(id+"F3.opExtrude","SWEPT_EDGE",EDGE,{"disambiguationData":[OSD([subQ1,subQ0]),TDD([makeQuery(id+"F0.imprint","INTERSECT",VERTEX,{"disambiguationData":[OD(0.0)],"derivedFrom":[subQ1,subQ0]})])]});}
            var Q16;
            {var subQ0=sQuery(id+"F0.wireOp",EDGE,"E3.right");var subQ1=sQuery(id+"F0.wireOp",EDGE,"E1.0");Q16=makeQuery(id+"F3.opExtrude","SWEPT_EDGE",EDGE,{"disambiguationData":[OSD([subQ1,subQ0]),TDD([makeQuery(id+"F0.imprint","INTERSECT",VERTEX,{"disambiguationData":[OD(1.0)],"derivedFrom":[subQ1,subQ0]})])]});}
            var Q17;
            {var subQ0=sQuery(id+"F0.wireOp",EDGE,"E2.right");var subQ1=sQuery(id+"F0.wireOp",EDGE,"E1.0");Q17=makeQuery(id+"F3.opExtrude","SWEPT_EDGE",EDGE,{"disambiguationData":[OSD([subQ1,subQ0]),TDD([makeQuery(id+"F0.imprint","INTERSECT",VERTEX,{"disambiguationData":[OD(1.0)],"derivedFrom":[subQ1,subQ0]})])]});}
            var Q18;
            {var subQ0=sQuery(id+"F0.wireOp",EDGE,"E3.right");var subQ1=sQuery(id+"F0.wireOp",EDGE,"E1.0");Q18=makeQuery(id+"F3.opExtrude","SWEPT_EDGE",EDGE,{"disambiguationData":[OSD([subQ1,subQ0]),TDD([makeQuery(id+"F0.imprint","INTERSECT",VERTEX,{"disambiguationData":[OD(0.0)],"derivedFrom":[subQ1,subQ0]})])]});}
            var Q19;
            {var subQ0=sQuery(id+"F0.wireOp",EDGE,"E2.right");var subQ1=sQuery(id+"F0.wireOp",EDGE,"E1.0");Q19=makeQuery(id+"F3.opExtrude","SWEPT_EDGE",EDGE,{"disambiguationData":[OSD([subQ1,subQ0]),TDD([makeQuery(id+"F0.imprint","INTERSECT",VERTEX,{"disambiguationData":[OD(0.0)],"derivedFrom":[subQ1,subQ0]})])]});}
            var Q20;
            {var subQ0=sQuery(id+"F0.wireOp",EDGE,"E8.left");var subQ1=sQuery(id+"F0.wireOp",EDGE,"E1.0");Q20=makeQuery(id+"F3.opExtrude","SWEPT_EDGE",EDGE,{"disambiguationData":[OSD([subQ1,subQ0]),TDD([makeQuery(id+"F0.imprint","INTERSECT",VERTEX,{"disambiguationData":[OD(1.0)],"derivedFrom":[subQ1,subQ0]})])]});}
            var Q21;
            {var subQ0=sQuery(id+"F0.wireOp",EDGE,"E9.left");var subQ1=sQuery(id+"F0.wireOp",EDGE,"E1.0");Q21=makeQuery(id+"F3.opExtrude","SWEPT_EDGE",EDGE,{"disambiguationData":[OSD([subQ1,subQ0]),TDD([makeQuery(id+"F0.imprint","INTERSECT",VERTEX,{"disambiguationData":[OD(1.0)],"derivedFrom":[subQ1,subQ0]})])]});}
            var Q22;
            {var subQ0=sQuery(id+"F0.wireOp",EDGE,"E7.top");var subQ1=sQuery(id+"F0.wireOp",EDGE,"E1.0");Q22=makeQuery(id+"F3.opExtrude","SWEPT_EDGE",EDGE,{"disambiguationData":[OSD([subQ1,subQ0]),TDD([makeQuery(id+"F0.imprint","INTERSECT",VERTEX,{"disambiguationData":[OD(1.0)],"derivedFrom":[subQ1,subQ0]})])]});}
            var Q23;
            {var subQ0=sQuery(id+"F0.wireOp",EDGE,"E6.bottom");var subQ1=sQuery(id+"F0.wireOp",EDGE,"E1.0");Q23=makeQuery(id+"F3.opExtrude","SWEPT_EDGE",EDGE,{"disambiguationData":[OSD([subQ1,subQ0]),TDD([makeQuery(id+"F0.imprint","INTERSECT",VERTEX,{"disambiguationData":[OD(0.0)],"derivedFrom":[subQ1,subQ0]})])]});}
            var Q24;
            {var subQ5=sQuery(id+"F0.wireOp",EDGE,"E6.bottom");var subQ8=sQuery(id+"F1.wireOp",EDGE,"E12");Q24=makeQuery(id+"F7.boolean.opBoolean","INTERSECT",EDGE,{"derivedFrom":[makeQuery(id+"F3.boolean.opBoolean","SPLIT",FACE,{"disambiguationData":[TD([makeQuery(id+"F3.opExtrude","SWEPT_FACE",FACE,{"disambiguationData":[OSD([subQ5])]})])],"derivedFrom":makeQuery(id+"F2.opExtrude","SWEPT_FACE",FACE,{"disambiguationData":[OSD([subQ8])]})}),makeQuery(id+"F7.opExtrude","SWEPT_FACE",FACE,{"disambiguationData":[OSD([sQuery(id+"F6.wireOp",EDGE,"E30")])]})]});}
            var Q25;
            Q25=makeQuery(id+"F7.boolean.opBoolean","INTERSECT",EDGE,{"derivedFrom":[makeQuery(id+"F3.opExtrude","SWEPT_FACE",FACE,{"disambiguationData":[OSD([sQuery(id+"F0.wireOp",EDGE,"E7.top")])]}),makeQuery(id+"F7.opExtrude","SWEPT_FACE",FACE,{"disambiguationData":[OSD([sQuery(id+"F6.wireOp",EDGE,"E30")])]})]});
            var Q26;
            {var subQ0=sQuery(id+"F0.wireOp",EDGE,"E1.0");var subQ1=sQuery(id+"F0.wireOp",EDGE,"E2.right");var subQ9=sQuery(id+"F1.wireOp",EDGE,"E12");Q26=makeQuery(id+"F7.boolean.opBoolean","INTERSECT",EDGE,{"disambiguationData":[OD(0.0)],"derivedFrom":[makeQuery(id+"F5.boolean.opBoolean","MERGE",FACE,{"derivedFrom":[makeQuery(id+"F3.boolean.opBoolean","SPLIT",FACE,{"disambiguationData":[TD([makeQuery(id+"F3.opExtrude","SWEPT_FACE",FACE,{"disambiguationData":[OSD([subQ1])]})])],"derivedFrom":makeQuery(id+"F2.opExtrude","SWEPT_FACE",FACE,{"disambiguationData":[OSD([subQ9])]})}),makeQuery(id+"F5.opExtrude","SWEPT_FACE",FACE,{"disambiguationData":[OSD([subQ0]),TDD([makeQuery(id+"F0.imprint","IMPRINT",EDGE,{"disambiguationData":[TD([[makeQuery(id+"F0.imprint","INTERSECT",VERTEX,{"disambiguationData":[OD(0.0)],"derivedFrom":[subQ0,sQuery(id+"F0.wireOp",EDGE,"E3.right")]}),1.0]])],"derivedFrom":subQ0})])]}),makeQuery(id+"F5.opExtrude","SWEPT_FACE",FACE,{"disambiguationData":[OSD([subQ0]),TDD([makeQuery(id+"F0.imprint","IMPRINT",EDGE,{"disambiguationData":[TD([[makeQuery(id+"F0.imprint","INTERSECT",VERTEX,{"disambiguationData":[OD(0.0)],"derivedFrom":[subQ0,sQuery(id+"F0.wireOp",EDGE,"E3.left")]}),-1.0]])],"derivedFrom":subQ0})])]})]}),makeQuery(id+"F7.opExtrude","SWEPT_FACE",FACE,{"disambiguationData":[OSD([sQuery(id+"F6.wireOp",EDGE,"E26")])]})]});}
            var Q27;
            Q27=makeQuery(id+"F7.boolean.opBoolean","INTERSECT",EDGE,{"derivedFrom":[makeQuery(id+"F5.boolean.opBoolean","COPY",FACE,{"derivedFrom":makeQuery(id+"F5.opExtrude","SWEPT_FACE",FACE,{"disambiguationData":[OSD([sQuery(id+"F0.wireOp",EDGE,"E3.right")])]})}),makeQuery(id+"F7.opExtrude","SWEPT_FACE",FACE,{"disambiguationData":[OSD([sQuery(id+"F6.wireOp",EDGE,"E26")])]})]});
            var Q28;
            Q28=makeQuery(id+"F7.boolean.opBoolean","INTERSECT",EDGE,{"derivedFrom":[makeQuery(id+"F4.opExtrude","CAP_FACE",FACE,{"disambiguationData":[OSD([sQuery(id+"F1.wireOp",EDGE,"E11")])],"isStart":false}),makeQuery(id+"F7.opExtrude","SWEPT_FACE",FACE,{"disambiguationData":[OSD([sQuery(id+"F6.wireOp",EDGE,"E26")])]})]});
            var Q29;
            {var subQ8=sQuery(id+"F1.wireOp",EDGE,"E12");var subQ10=sQuery(id+"F0.wireOp",EDGE,"E2.left");Q29=makeQuery(id+"F7.boolean.opBoolean","INTERSECT",EDGE,{"disambiguationData":[OD(0.0)],"derivedFrom":[makeQuery(id+"F3.boolean.opBoolean","SPLIT",FACE,{"disambiguationData":[TD([makeQuery(id+"F3.opExtrude","SWEPT_FACE",FACE,{"disambiguationData":[OSD([subQ10])]})])],"derivedFrom":makeQuery(id+"F2.opExtrude","SWEPT_FACE",FACE,{"disambiguationData":[OSD([subQ8])]})}),makeQuery(id+"F7.opExtrude","SWEPT_FACE",FACE,{"disambiguationData":[OSD([sQuery(id+"F6.wireOp",EDGE,"E25")])]})]});}
            var Q30;
            {var subQ8=sQuery(id+"F1.wireOp",EDGE,"E12");var subQ10=sQuery(id+"F0.wireOp",EDGE,"E2.left");Q30=makeQuery(id+"F7.boolean.opBoolean","INTERSECT",EDGE,{"disambiguationData":[OD(1.0)],"derivedFrom":[makeQuery(id+"F3.boolean.opBoolean","SPLIT",FACE,{"disambiguationData":[TD([makeQuery(id+"F3.opExtrude","SWEPT_FACE",FACE,{"disambiguationData":[OSD([subQ10])]})])],"derivedFrom":makeQuery(id+"F2.opExtrude","SWEPT_FACE",FACE,{"disambiguationData":[OSD([subQ8])]})}),makeQuery(id+"F7.opExtrude","SWEPT_FACE",FACE,{"disambiguationData":[OSD([sQuery(id+"F6.wireOp",EDGE,"E25")])]})]});}
            var Q31;
            {var subQ0=sQuery(id+"F0.wireOp",EDGE,"E1.0");var subQ1=sQuery(id+"F0.wireOp",EDGE,"E2.right");var subQ9=sQuery(id+"F1.wireOp",EDGE,"E12");Q31=makeQuery(id+"F7.boolean.opBoolean","INTERSECT",EDGE,{"disambiguationData":[OD(1.0)],"derivedFrom":[makeQuery(id+"F5.boolean.opBoolean","MERGE",FACE,{"derivedFrom":[makeQuery(id+"F3.boolean.opBoolean","SPLIT",FACE,{"disambiguationData":[TD([makeQuery(id+"F3.opExtrude","SWEPT_FACE",FACE,{"disambiguationData":[OSD([subQ1])]})])],"derivedFrom":makeQuery(id+"F2.opExtrude","SWEPT_FACE",FACE,{"disambiguationData":[OSD([subQ9])]})}),makeQuery(id+"F5.opExtrude","SWEPT_FACE",FACE,{"disambiguationData":[OSD([subQ0]),TDD([makeQuery(id+"F0.imprint","IMPRINT",EDGE,{"disambiguationData":[TD([[makeQuery(id+"F0.imprint","INTERSECT",VERTEX,{"disambiguationData":[OD(0.0)],"derivedFrom":[subQ0,sQuery(id+"F0.wireOp",EDGE,"E3.right")]}),1.0]])],"derivedFrom":subQ0})])]}),makeQuery(id+"F5.opExtrude","SWEPT_FACE",FACE,{"disambiguationData":[OSD([subQ0]),TDD([makeQuery(id+"F0.imprint","IMPRINT",EDGE,{"disambiguationData":[TD([[makeQuery(id+"F0.imprint","INTERSECT",VERTEX,{"disambiguationData":[OD(0.0)],"derivedFrom":[subQ0,sQuery(id+"F0.wireOp",EDGE,"E3.left")]}),-1.0]])],"derivedFrom":subQ0})])]})]}),makeQuery(id+"F7.opExtrude","SWEPT_FACE",FACE,{"disambiguationData":[OSD([sQuery(id+"F6.wireOp",EDGE,"E26")])]})]});}
            var Q32;
            Q32=makeQuery(id+"F7.boolean.opBoolean","INTERSECT",EDGE,{"derivedFrom":[makeQuery(id+"F5.boolean.opBoolean","COPY",FACE,{"derivedFrom":makeQuery(id+"F5.opExtrude","SWEPT_FACE",FACE,{"disambiguationData":[OSD([sQuery(id+"F0.wireOp",EDGE,"E3.left")])]})}),makeQuery(id+"F7.opExtrude","SWEPT_FACE",FACE,{"disambiguationData":[OSD([sQuery(id+"F6.wireOp",EDGE,"E26")])]})]});
            var Q33;
            Q33=makeQuery(id+"F5.boolean.opBoolean","COPY",EDGE,{"derivedFrom":makeQuery(id+"F5.opExtrude","SWEPT_EDGE",EDGE,{"disambiguationData":[OSD([sQuery(id+"F0.wireOp",EDGE,"E1.0"),sQuery(id+"F0.wireOp",EDGE,"E6.bottom")])]})});
            var Q34;
            {var subQ0=sQuery(id+"F0.wireOp",EDGE,"E1.0");var subQ1=sQuery(id+"F0.wireOp",EDGE,"E2.right");var subQ9=sQuery(id+"F1.wireOp",EDGE,"E12");Q34=makeQuery(id+"F7.boolean.opBoolean","INTERSECT",EDGE,{"disambiguationData":[OD(1.0)],"derivedFrom":[makeQuery(id+"F5.boolean.opBoolean","MERGE",FACE,{"derivedFrom":[makeQuery(id+"F3.boolean.opBoolean","SPLIT",FACE,{"disambiguationData":[TD([makeQuery(id+"F3.opExtrude","SWEPT_FACE",FACE,{"disambiguationData":[OSD([subQ1])]})])],"derivedFrom":makeQuery(id+"F2.opExtrude","SWEPT_FACE",FACE,{"disambiguationData":[OSD([subQ9])]})}),makeQuery(id+"F5.opExtrude","SWEPT_FACE",FACE,{"disambiguationData":[OSD([subQ0]),TDD([makeQuery(id+"F0.imprint","IMPRINT",EDGE,{"disambiguationData":[TD([[makeQuery(id+"F0.imprint","INTERSECT",VERTEX,{"disambiguationData":[OD(0.0)],"derivedFrom":[subQ0,sQuery(id+"F0.wireOp",EDGE,"E3.right")]}),1.0]])],"derivedFrom":subQ0})])]}),makeQuery(id+"F5.opExtrude","SWEPT_FACE",FACE,{"disambiguationData":[OSD([subQ0]),TDD([makeQuery(id+"F0.imprint","IMPRINT",EDGE,{"disambiguationData":[TD([[makeQuery(id+"F0.imprint","INTERSECT",VERTEX,{"disambiguationData":[OD(0.0)],"derivedFrom":[subQ0,sQuery(id+"F0.wireOp",EDGE,"E3.left")]}),-1.0]])],"derivedFrom":subQ0})])]})]}),makeQuery(id+"F7.opExtrude","SWEPT_FACE",FACE,{"disambiguationData":[OSD([sQuery(id+"F6.wireOp",EDGE,"E27")])]})]});}
            var Q35;
            {var subQ0=sQuery(id+"F0.wireOp",EDGE,"E1.0");var subQ1=sQuery(id+"F0.wireOp",EDGE,"E2.right");var subQ9=sQuery(id+"F1.wireOp",EDGE,"E12");Q35=makeQuery(id+"F7.boolean.opBoolean","INTERSECT",EDGE,{"disambiguationData":[OD(0.0)],"derivedFrom":[makeQuery(id+"F5.boolean.opBoolean","MERGE",FACE,{"derivedFrom":[makeQuery(id+"F3.boolean.opBoolean","SPLIT",FACE,{"disambiguationData":[TD([makeQuery(id+"F3.opExtrude","SWEPT_FACE",FACE,{"disambiguationData":[OSD([subQ1])]})])],"derivedFrom":makeQuery(id+"F2.opExtrude","SWEPT_FACE",FACE,{"disambiguationData":[OSD([subQ9])]})}),makeQuery(id+"F5.opExtrude","SWEPT_FACE",FACE,{"disambiguationData":[OSD([subQ0]),TDD([makeQuery(id+"F0.imprint","IMPRINT",EDGE,{"disambiguationData":[TD([[makeQuery(id+"F0.imprint","INTERSECT",VERTEX,{"disambiguationData":[OD(0.0)],"derivedFrom":[subQ0,sQuery(id+"F0.wireOp",EDGE,"E3.right")]}),1.0]])],"derivedFrom":subQ0})])]}),makeQuery(id+"F5.opExtrude","SWEPT_FACE",FACE,{"disambiguationData":[OSD([subQ0]),TDD([makeQuery(id+"F0.imprint","IMPRINT",EDGE,{"disambiguationData":[TD([[makeQuery(id+"F0.imprint","INTERSECT",VERTEX,{"disambiguationData":[OD(0.0)],"derivedFrom":[subQ0,sQuery(id+"F0.wireOp",EDGE,"E3.left")]}),-1.0]])],"derivedFrom":subQ0})])]})]}),makeQuery(id+"F7.opExtrude","SWEPT_FACE",FACE,{"disambiguationData":[OSD([sQuery(id+"F6.wireOp",EDGE,"E27")])]})]});}
            var Q36;
            Q36=makeQuery(id+"F7.boolean.opBoolean","INTERSECT",EDGE,{"derivedFrom":[makeQuery(id+"F3.opExtrude","SWEPT_FACE",FACE,{"disambiguationData":[OSD([sQuery(id+"F0.wireOp",EDGE,"E7.bottom")])]}),makeQuery(id+"F7.opExtrude","SWEPT_FACE",FACE,{"disambiguationData":[OSD([sQuery(id+"F6.wireOp",EDGE,"E30")])]})]});
            var Q37;
            {var subQ8=sQuery(id+"F1.wireOp",EDGE,"E12");var subQ10=sQuery(id+"F0.wireOp",EDGE,"E2.left");Q37=makeQuery(id+"F7.boolean.opBoolean","INTERSECT",EDGE,{"derivedFrom":[makeQuery(id+"F3.boolean.opBoolean","SPLIT",FACE,{"disambiguationData":[TD([makeQuery(id+"F3.opExtrude","SWEPT_FACE",FACE,{"disambiguationData":[OSD([subQ10])]})])],"derivedFrom":makeQuery(id+"F2.opExtrude","SWEPT_FACE",FACE,{"disambiguationData":[OSD([subQ8])]})}),makeQuery(id+"F7.opExtrude","SWEPT_FACE",FACE,{"disambiguationData":[OSD([sQuery(id+"F6.wireOp",EDGE,"E30")])]})]});}
            var Q38;
            {var subQ4=sQuery(id+"F0.wireOp",EDGE,"E6.top");var subQ8=sQuery(id+"F1.wireOp",EDGE,"E12");Q38=makeQuery(id+"F7.boolean.opBoolean","INTERSECT",EDGE,{"disambiguationData":[OD(0.0)],"derivedFrom":[makeQuery(id+"F3.boolean.opBoolean","SPLIT",FACE,{"disambiguationData":[TD([makeQuery(id+"F3.opExtrude","SWEPT_FACE",FACE,{"disambiguationData":[OSD([subQ4])]})])],"derivedFrom":makeQuery(id+"F2.opExtrude","SWEPT_FACE",FACE,{"disambiguationData":[OSD([subQ8])]})}),makeQuery(id+"F7.opExtrude","SWEPT_FACE",FACE,{"disambiguationData":[OSD([sQuery(id+"F6.wireOp",EDGE,"E29")])]})]});}
            var Q39;
            {var subQ4=sQuery(id+"F0.wireOp",EDGE,"E6.top");var subQ8=sQuery(id+"F1.wireOp",EDGE,"E12");Q39=makeQuery(id+"F7.boolean.opBoolean","INTERSECT",EDGE,{"disambiguationData":[OD(1.0)],"derivedFrom":[makeQuery(id+"F3.boolean.opBoolean","SPLIT",FACE,{"disambiguationData":[TD([makeQuery(id+"F3.opExtrude","SWEPT_FACE",FACE,{"disambiguationData":[OSD([subQ4])]})])],"derivedFrom":makeQuery(id+"F2.opExtrude","SWEPT_FACE",FACE,{"disambiguationData":[OSD([subQ8])]})}),makeQuery(id+"F7.opExtrude","SWEPT_FACE",FACE,{"disambiguationData":[OSD([sQuery(id+"F6.wireOp",EDGE,"E29")])]})]});}
            var Q40;
            {var subQ0=sQuery(id+"F0.wireOp",EDGE,"E8.right");Q40=makeQuery(id+"F7.boolean.opBoolean","INTERSECT",EDGE,{"derivedFrom":[makeQuery(id+"F5.boolean.opBoolean","MERGE",FACE,{"derivedFrom":[makeQuery(id+"F3.opExtrude","SWEPT_FACE",FACE,{"disambiguationData":[OSD([subQ0])]}),makeQuery(id+"F5.opExtrude","SWEPT_FACE",FACE,{"disambiguationData":[OSD([subQ0])]})]}),makeQuery(id+"F7.opExtrude","SWEPT_FACE",FACE,{"disambiguationData":[OSD([sQuery(id+"F6.wireOp",EDGE,"E28")])]})]});}
            var Q41;
            {var subQ0=sQuery(id+"F0.wireOp",EDGE,"E8.right");var subQ1=sQuery(id+"F0.wireOp",EDGE,"E1.0");var subQ9=sQuery(id+"F1.wireOp",EDGE,"E12");Q41=makeQuery(id+"F7.boolean.opBoolean","INTERSECT",EDGE,{"derivedFrom":[makeQuery(id+"F5.boolean.opBoolean","MERGE",FACE,{"derivedFrom":[makeQuery(id+"F3.boolean.opBoolean","SPLIT",FACE,{"disambiguationData":[TD([makeQuery(id+"F3.opExtrude","SWEPT_FACE",FACE,{"disambiguationData":[OSD([subQ0])]})])],"derivedFrom":makeQuery(id+"F2.opExtrude","SWEPT_FACE",FACE,{"disambiguationData":[OSD([subQ9])]})}),makeQuery(id+"F5.opExtrude","SWEPT_FACE",FACE,{"disambiguationData":[OSD([subQ1]),TDD([makeQuery(id+"F0.imprint","IMPRINT",EDGE,{"disambiguationData":[TD([[makeQuery(id+"F0.imprint","INTERSECT",VERTEX,{"disambiguationData":[OD(1.0)],"derivedFrom":[subQ1,subQ0]}),-1.0]])],"derivedFrom":subQ1})])]})]}),makeQuery(id+"F7.opExtrude","SWEPT_FACE",FACE,{"disambiguationData":[OSD([sQuery(id+"F6.wireOp",EDGE,"E28")])]})]});}
            var Q42;
            {var subQ4=sQuery(id+"F0.wireOp",EDGE,"E6.top");var subQ8=sQuery(id+"F1.wireOp",EDGE,"E12");Q42=makeQuery(id+"F7.boolean.opBoolean","INTERSECT",EDGE,{"derivedFrom":[makeQuery(id+"F3.boolean.opBoolean","SPLIT",FACE,{"disambiguationData":[TD([makeQuery(id+"F3.opExtrude","SWEPT_FACE",FACE,{"disambiguationData":[OSD([subQ4])]})])],"derivedFrom":makeQuery(id+"F2.opExtrude","SWEPT_FACE",FACE,{"disambiguationData":[OSD([subQ8])]})}),makeQuery(id+"F7.opExtrude","SWEPT_FACE",FACE,{"disambiguationData":[OSD([sQuery(id+"F6.wireOp",EDGE,"E28")])]})]});}
            var Q43;
            Q43=makeQuery(id+"F7.boolean.opBoolean","INTERSECT",EDGE,{"derivedFrom":[makeQuery(id+"F3.opExtrude","SWEPT_FACE",FACE,{"disambiguationData":[OSD([sQuery(id+"F0.wireOp",EDGE,"E8.left")])]}),makeQuery(id+"F7.opExtrude","SWEPT_FACE",FACE,{"disambiguationData":[OSD([sQuery(id+"F6.wireOp",EDGE,"E28")])]})]});
            fillet(context, id + "F8", {"entities" : qUnion([Q0, Q1, Q2, Q3, Q4, Q5, Q6, Q7, Q8, Q9, Q10, Q11, Q12, Q13, Q14, Q15, Q16, Q17, Q18, Q19, Q20, Q21, Q22, Q23, Q24, Q25, Q26, Q27, Q28, Q29, Q30, Q31, Q32, Q33, Q34, Q35, Q36, Q37, Q38, Q39, Q40, Q41, Q42, Q43]), "radius" : 1 * mm, "tangentPropagation" : true, "allowEdgeOverflow" : false});
        }
        {
            var Q0;
            {var subQ0=sQuery(id+"F6.wireOp",EDGE,"E31");var subQ1=sQuery(id+"F6.wireOp",EDGE,"E13");var subQ2=makeQuery(id+"F6.imprint","INTERSECT",VERTEX,{"disambiguationData":[OD(0.0)],"derivedFrom":[subQ1,subQ0]});Q0=makeQuery(id+"F6.imprint","IMPRINT",FACE,{"disambiguationData":[TD([[makeQuery(id+"F6.imprint","IMPRINT",EDGE,{"disambiguationData":[TD([[subQ2,-1.0]])],"derivedFrom":subQ1}),-1.0]])]});}
            var Q1;
            {var subQ0=sQuery(id+"F6.wireOp",EDGE,"E31");var subQ1=sQuery(id+"F6.wireOp",EDGE,"E13");var subQ2=makeQuery(id+"F6.imprint","INTERSECT",VERTEX,{"disambiguationData":[OD(0.0)],"derivedFrom":[subQ1,subQ0]});Q1=makeQuery(id+"F6.imprint","IMPRINT",FACE,{"disambiguationData":[TD([[makeQuery(id+"F6.imprint","IMPRINT",EDGE,{"disambiguationData":[TD([[subQ2,-1.0]])],"derivedFrom":subQ1}),1.0]])]});}
            var Q2;
            {var subQ0=sQuery(id+"F6.wireOp",EDGE,"E32");var subQ1=sQuery(id+"F6.wireOp",EDGE,"E13");var subQ2=makeQuery(id+"F6.imprint","INTERSECT",VERTEX,{"disambiguationData":[OD(0.0)],"derivedFrom":[subQ1,subQ0]});Q2=makeQuery(id+"F6.imprint","IMPRINT",FACE,{"disambiguationData":[TD([[makeQuery(id+"F6.imprint","IMPRINT",EDGE,{"disambiguationData":[TD([[subQ2,-1.0]])],"derivedFrom":subQ1}),-1.0]])]});}
            var Q3;
            {var subQ0=sQuery(id+"F6.wireOp",EDGE,"E32");var subQ1=sQuery(id+"F6.wireOp",EDGE,"E13");var subQ2=makeQuery(id+"F6.imprint","INTERSECT",VERTEX,{"disambiguationData":[OD(0.0)],"derivedFrom":[subQ1,subQ0]});Q3=makeQuery(id+"F6.imprint","IMPRINT",FACE,{"disambiguationData":[TD([[makeQuery(id+"F6.imprint","IMPRINT",EDGE,{"disambiguationData":[TD([[subQ2,-1.0]])],"derivedFrom":subQ1}),1.0]])]});}
            var Q4;
            {var subQ0=sQuery(id+"F6.wireOp",EDGE,"E33");var subQ1=sQuery(id+"F6.wireOp",EDGE,"E13");var subQ2=makeQuery(id+"F6.imprint","INTERSECT",VERTEX,{"disambiguationData":[OD(0.0)],"derivedFrom":[subQ1,subQ0]});Q4=makeQuery(id+"F6.imprint","IMPRINT",FACE,{"disambiguationData":[TD([[makeQuery(id+"F6.imprint","IMPRINT",EDGE,{"disambiguationData":[TD([[subQ2,-1.0]])],"derivedFrom":subQ1}),1.0]])]});}
            var Q5;
            {var subQ0=sQuery(id+"F6.wireOp",EDGE,"E33");var subQ1=sQuery(id+"F6.wireOp",EDGE,"E13");var subQ2=makeQuery(id+"F6.imprint","INTERSECT",VERTEX,{"disambiguationData":[OD(0.0)],"derivedFrom":[subQ1,subQ0]});Q5=makeQuery(id+"F6.imprint","IMPRINT",FACE,{"disambiguationData":[TD([[makeQuery(id+"F6.imprint","IMPRINT",EDGE,{"disambiguationData":[TD([[subQ2,-1.0]])],"derivedFrom":subQ1}),-1.0]])]});}
            var Q6;
            {var subQ0=sQuery(id+"F6.wireOp",EDGE,"E34");var subQ1=sQuery(id+"F6.wireOp",EDGE,"E13");var subQ2=makeQuery(id+"F6.imprint","INTERSECT",VERTEX,{"disambiguationData":[OD(0.0)],"derivedFrom":[subQ1,subQ0]});Q6=makeQuery(id+"F6.imprint","IMPRINT",FACE,{"disambiguationData":[TD([[makeQuery(id+"F6.imprint","IMPRINT",EDGE,{"disambiguationData":[TD([[subQ2,-1.0]])],"derivedFrom":subQ1}),1.0]])]});}
            var Q7;
            {var subQ0=sQuery(id+"F6.wireOp",EDGE,"E34");var subQ1=sQuery(id+"F6.wireOp",EDGE,"E13");var subQ2=makeQuery(id+"F6.imprint","INTERSECT",VERTEX,{"disambiguationData":[OD(0.0)],"derivedFrom":[subQ1,subQ0]});Q7=makeQuery(id+"F6.imprint","IMPRINT",FACE,{"disambiguationData":[TD([[makeQuery(id+"F6.imprint","IMPRINT",EDGE,{"disambiguationData":[TD([[subQ2,-1.0]])],"derivedFrom":subQ1}),-1.0]])]});}
            var Q8;
            {var subQ1=sQuery(id+"F6.wireOp",EDGE,"E36.bottom");Q8=makeQuery(id+"F6.imprint","IMPRINT",FACE,{"disambiguationData":[TD([[makeQuery(id+"F6.imprint","IMPRINT",EDGE,{"derivedFrom":subQ1}),-1.0]])]});}
            var Q9;
            {var subQ0=sQuery(id+"F6.wireOp",EDGE,"E36.top");var subQ1=sQuery(id+"F6.wireOp",EDGE,"E13");var subQ2=makeQuery(id+"F6.imprint","INTERSECT",VERTEX,{"derivedFrom":[subQ1,subQ0]});Q9=makeQuery(id+"F6.imprint","IMPRINT",FACE,{"disambiguationData":[TD([[makeQuery(id+"F6.imprint","IMPRINT",EDGE,{"disambiguationData":[TD([[subQ2,-1.0]])],"derivedFrom":subQ1}),1.0]])]});}
            var Q10;
            {var subQ0=sQuery(id+"F6.wireOp",EDGE,"E35");var subQ1=sQuery(id+"F6.wireOp",EDGE,"E13");var subQ2=makeQuery(id+"F6.imprint","INTERSECT",VERTEX,{"disambiguationData":[OD(0.0)],"derivedFrom":[subQ1,subQ0]});Q10=makeQuery(id+"F6.imprint","IMPRINT",FACE,{"disambiguationData":[TD([[makeQuery(id+"F6.imprint","IMPRINT",EDGE,{"disambiguationData":[TD([[subQ2,-1.0]])],"derivedFrom":subQ1}),-1.0]])]});}
            var Q11;
            {var subQ0=sQuery(id+"F6.wireOp",EDGE,"E35");var subQ1=sQuery(id+"F6.wireOp",EDGE,"E13");var subQ2=makeQuery(id+"F6.imprint","INTERSECT",VERTEX,{"disambiguationData":[OD(0.0)],"derivedFrom":[subQ1,subQ0]});Q11=makeQuery(id+"F6.imprint","IMPRINT",FACE,{"disambiguationData":[TD([[makeQuery(id+"F6.imprint","IMPRINT",EDGE,{"disambiguationData":[TD([[subQ2,-1.0]])],"derivedFrom":subQ1}),1.0]])]});}
            extrude(context, id + "F9", {"entities" : qUnion([Q0, Q1, Q2, Q3, Q4, Q5, Q6, Q7, Q8, Q9, Q10, Q11]), "operationType" : NewBodyOperationType.ADD, "depth" : 11 * mm, "offsetDistance" : 25 * mm, "hasDraft" : true, "draftAngle" : .9 * degree, "draftPullDirection" : true});
        }
        {
            var Q0;
            {var subQ0=sQuery(id+"F6.wireOp",EDGE,"E35");var subQ1=sQuery(id+"F6.wireOp",EDGE,"E13");var subQ2=makeQuery(id+"F6.imprint","INTERSECT",VERTEX,{"disambiguationData":[OD(0.0)],"derivedFrom":[subQ1,subQ0]});Q0=makeQuery(id+"F6.imprint","IMPRINT",FACE,{"disambiguationData":[TD([[makeQuery(id+"F6.imprint","IMPRINT",EDGE,{"disambiguationData":[TD([[subQ2,-1.0]])],"derivedFrom":subQ1}),-1.0]])]});}
            var Q1;
            {var subQ0=sQuery(id+"F6.wireOp",EDGE,"E35");var subQ1=sQuery(id+"F6.wireOp",EDGE,"E13");var subQ2=makeQuery(id+"F6.imprint","INTERSECT",VERTEX,{"disambiguationData":[OD(0.0)],"derivedFrom":[subQ1,subQ0]});Q1=makeQuery(id+"F6.imprint","IMPRINT",FACE,{"disambiguationData":[TD([[makeQuery(id+"F6.imprint","IMPRINT",EDGE,{"disambiguationData":[TD([[subQ2,-1.0]])],"derivedFrom":subQ1}),1.0]])]});}
            var Q2;
            {var subQ1=sQuery(id+"F6.wireOp",EDGE,"E36.bottom");Q2=makeQuery(id+"F6.imprint","IMPRINT",FACE,{"disambiguationData":[TD([[makeQuery(id+"F6.imprint","IMPRINT",EDGE,{"derivedFrom":subQ1}),-1.0]])]});}
            var Q3;
            {var subQ0=sQuery(id+"F6.wireOp",EDGE,"E36.top");var subQ1=sQuery(id+"F6.wireOp",EDGE,"E13");var subQ2=makeQuery(id+"F6.imprint","INTERSECT",VERTEX,{"derivedFrom":[subQ1,subQ0]});Q3=makeQuery(id+"F6.imprint","IMPRINT",FACE,{"disambiguationData":[TD([[makeQuery(id+"F6.imprint","IMPRINT",EDGE,{"disambiguationData":[TD([[subQ2,-1.0]])],"derivedFrom":subQ1}),1.0]])]});}
            var Q4;
            {var subQ0=sQuery(id+"F6.wireOp",EDGE,"E34");var subQ1=sQuery(id+"F6.wireOp",EDGE,"E13");var subQ2=makeQuery(id+"F6.imprint","INTERSECT",VERTEX,{"disambiguationData":[OD(0.0)],"derivedFrom":[subQ1,subQ0]});Q4=makeQuery(id+"F6.imprint","IMPRINT",FACE,{"disambiguationData":[TD([[makeQuery(id+"F6.imprint","IMPRINT",EDGE,{"disambiguationData":[TD([[subQ2,-1.0]])],"derivedFrom":subQ1}),1.0]])]});}
            var Q5;
            {var subQ0=sQuery(id+"F6.wireOp",EDGE,"E34");var subQ1=sQuery(id+"F6.wireOp",EDGE,"E13");var subQ2=makeQuery(id+"F6.imprint","INTERSECT",VERTEX,{"disambiguationData":[OD(0.0)],"derivedFrom":[subQ1,subQ0]});Q5=makeQuery(id+"F6.imprint","IMPRINT",FACE,{"disambiguationData":[TD([[makeQuery(id+"F6.imprint","IMPRINT",EDGE,{"disambiguationData":[TD([[subQ2,-1.0]])],"derivedFrom":subQ1}),-1.0]])]});}
            var Q6;
            {var subQ0=sQuery(id+"F6.wireOp",EDGE,"E33");var subQ1=sQuery(id+"F6.wireOp",EDGE,"E13");var subQ2=makeQuery(id+"F6.imprint","INTERSECT",VERTEX,{"disambiguationData":[OD(0.0)],"derivedFrom":[subQ1,subQ0]});Q6=makeQuery(id+"F6.imprint","IMPRINT",FACE,{"disambiguationData":[TD([[makeQuery(id+"F6.imprint","IMPRINT",EDGE,{"disambiguationData":[TD([[subQ2,-1.0]])],"derivedFrom":subQ1}),1.0]])]});}
            var Q7;
            {var subQ0=sQuery(id+"F6.wireOp",EDGE,"E33");var subQ1=sQuery(id+"F6.wireOp",EDGE,"E13");var subQ2=makeQuery(id+"F6.imprint","INTERSECT",VERTEX,{"disambiguationData":[OD(0.0)],"derivedFrom":[subQ1,subQ0]});Q7=makeQuery(id+"F6.imprint","IMPRINT",FACE,{"disambiguationData":[TD([[makeQuery(id+"F6.imprint","IMPRINT",EDGE,{"disambiguationData":[TD([[subQ2,-1.0]])],"derivedFrom":subQ1}),-1.0]])]});}
            var Q8;
            {var subQ0=sQuery(id+"F6.wireOp",EDGE,"E32");var subQ1=sQuery(id+"F6.wireOp",EDGE,"E13");var subQ2=makeQuery(id+"F6.imprint","INTERSECT",VERTEX,{"disambiguationData":[OD(0.0)],"derivedFrom":[subQ1,subQ0]});Q8=makeQuery(id+"F6.imprint","IMPRINT",FACE,{"disambiguationData":[TD([[makeQuery(id+"F6.imprint","IMPRINT",EDGE,{"disambiguationData":[TD([[subQ2,-1.0]])],"derivedFrom":subQ1}),1.0]])]});}
            var Q9;
            {var subQ0=sQuery(id+"F6.wireOp",EDGE,"E32");var subQ1=sQuery(id+"F6.wireOp",EDGE,"E13");var subQ2=makeQuery(id+"F6.imprint","INTERSECT",VERTEX,{"disambiguationData":[OD(0.0)],"derivedFrom":[subQ1,subQ0]});Q9=makeQuery(id+"F6.imprint","IMPRINT",FACE,{"disambiguationData":[TD([[makeQuery(id+"F6.imprint","IMPRINT",EDGE,{"disambiguationData":[TD([[subQ2,-1.0]])],"derivedFrom":subQ1}),-1.0]])]});}
            var Q10;
            {var subQ0=sQuery(id+"F6.wireOp",EDGE,"E31");var subQ1=sQuery(id+"F6.wireOp",EDGE,"E13");var subQ2=makeQuery(id+"F6.imprint","INTERSECT",VERTEX,{"disambiguationData":[OD(0.0)],"derivedFrom":[subQ1,subQ0]});Q10=makeQuery(id+"F6.imprint","IMPRINT",FACE,{"disambiguationData":[TD([[makeQuery(id+"F6.imprint","IMPRINT",EDGE,{"disambiguationData":[TD([[subQ2,-1.0]])],"derivedFrom":subQ1}),-1.0]])]});}
            var Q11;
            {var subQ0=sQuery(id+"F6.wireOp",EDGE,"E31");var subQ1=sQuery(id+"F6.wireOp",EDGE,"E13");var subQ2=makeQuery(id+"F6.imprint","INTERSECT",VERTEX,{"disambiguationData":[OD(0.0)],"derivedFrom":[subQ1,subQ0]});Q11=makeQuery(id+"F6.imprint","IMPRINT",FACE,{"disambiguationData":[TD([[makeQuery(id+"F6.imprint","IMPRINT",EDGE,{"disambiguationData":[TD([[subQ2,-1.0]])],"derivedFrom":subQ1}),1.0]])]});}
            extrude(context, id + "F10", {"entities" : qUnion([Q0, Q1, Q2, Q3, Q4, Q5, Q6, Q7, Q8, Q9, Q10, Q11]), "operationType" : NewBodyOperationType.REMOVE, "depth" : 3 * mm, "offsetDistance" : 25 * mm});
        }
        {
            var Q0;
            Q0=qCreatedBy(makeId("Top.planeOp"),FACE);
            var sketch = newSketch(context, id + "F11", { "sketchPlane" : qUnion([Q0])});
            skCircle(sketch, "E37", {"center": v(0, 0) * mm, "radius": 17.33 * mm});
            skSolve(sketch);
        }
        {
            var Q0;
            Q0=makeQuery(id+"F11.imprint","IMPRINT",FACE,{"disambiguationData":[TD([[makeQuery(id+"F11.imprint","IMPRINT",EDGE,{"derivedFrom":sQuery(id+"F11.wireOp",EDGE,"E37")}),1.0]])]});
            extrude(context, id + "F12", {"entities" : qUnion([Q0]), "operationType" : NewBodyOperationType.REMOVE, "depth" : 1 * mm, "offsetDistance" : 25 * mm});
        }
        {
            var Q0;
            Q0=makeQuery(id+"F9.opExtrude","CAP_EDGE",EDGE,{"disambiguationData":[OSD([sQuery(id+"F6.wireOp",EDGE,"E34")])],"isStart":false});
            var Q1;
            Q1=makeQuery(id+"F9.opExtrude","CAP_EDGE",EDGE,{"disambiguationData":[OSD([sQuery(id+"F6.wireOp",EDGE,"E33")])],"isStart":false});
            var Q2;
            Q2=makeQuery(id+"F9.opExtrude","CAP_EDGE",EDGE,{"disambiguationData":[OSD([sQuery(id+"F6.wireOp",EDGE,"E32")])],"isStart":false});
            var Q3;
            Q3=makeQuery(id+"F9.opExtrude","CAP_EDGE",EDGE,{"disambiguationData":[OSD([sQuery(id+"F6.wireOp",EDGE,"E31")])],"isStart":false});
            var Q4;
            Q4=makeQuery(id+"F9.opExtrude","CAP_EDGE",EDGE,{"disambiguationData":[OSD([sQuery(id+"F6.wireOp",EDGE,"E35")])],"isStart":false});
            var Q5;
            Q5=makeQuery(id+"F9.opExtrude","CAP_EDGE",EDGE,{"disambiguationData":[OSD([sQuery(id+"F6.wireOp",EDGE,"E36.bottom")])],"isStart":false});
            var Q6;
            Q6=makeQuery(id+"F9.opExtrude","CAP_EDGE",EDGE,{"disambiguationData":[OSD([sQuery(id+"F6.wireOp",EDGE,"E36.right")])],"isStart":false});
            var Q7;
            Q7=makeQuery(id+"F9.opExtrude","CAP_EDGE",EDGE,{"disambiguationData":[OSD([sQuery(id+"F6.wireOp",EDGE,"E36.top")])],"isStart":false});
            var Q8;
            Q8=makeQuery(id+"F9.opExtrude","CAP_EDGE",EDGE,{"disambiguationData":[OSD([sQuery(id+"F6.wireOp",EDGE,"E36.left")])],"isStart":false});
            fillet(context, id + "F13", {"entities" : qUnion([Q0, Q1, Q2, Q3, Q4, Q5, Q6, Q7, Q8]), "radius" : .45 * mm, "tangentPropagation" : true, "allowEdgeOverflow" : false});
        }
    });
